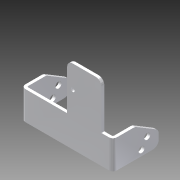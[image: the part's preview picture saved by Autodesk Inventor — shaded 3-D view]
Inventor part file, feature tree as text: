
AUTODESK INVENTOR PART (.ipt)
format: ipt  version: 2014 SP1 (Build 180222100, 222)  size: 293,888 bytes
history: native  units: in
note: dims shown in document units (in); Inventor stores cm internally (conversion verified against a paired STEP export)
features: other x8, sketch x5, sheet_metal_op x3, chamfer x2
ambient origin geometry x8: Origin, YZ Plane, XZ Plane, XY Plane, X Axis, Y Axis, Z Axis, Center Point
bodies: Solid1 (feature_tree)
feature tree (18):
  sheet_metal_op  "Face1"
  sheet_metal_op  "Flange1"
  chamfer  "Corner Round1"
  chamfer  "Corner Round2"
  sketch  "Sketch1"  dims[d0=0.155in]
  other  "Plate1"
  sketch  "Sketch2"  dims[d1=2.0in]
  other  "Plate2"
  sheet_metal_op  "Bend1"
  other  "mSketch3"
  sketch  "Sketch4"  dims[d3=1.25in]
  sketch  "Sketch5"  dims[d4=3.75in]
  sketch  "Sketch6"  dims[d6=0.375in d7=1.5in d8=0.25in d9=1.0in d10=0.125in d11=0.125in d12=0.0625in d13=0.25in d14=0.125in d15=2.0in d16=90.0deg d17=0.05in d18=0.5in d19=0.125in d20=0.125in d21=0.25in d22=0.266in d23=0.5in d24=0.125in d25=0.0in d26=0.266in d27=0.5in d28=0.125in d29=0.0in d30=0.75in d31=0.25in d32=0.266in d33=0.75in d34=0.25in d35=0.875in d36=0.625in d37=1.1811in d39=1.25in d40=0.3937in d42=1.0in d44=0.125in d45=0.0in d46=0.125in d47=0.0in d48=0.25in d2=0.25in d5=0.25in]
  other  "Cut1"
  other  "Cut2"
  other  "Cut3"
  other  "Cut4"
  other  "Definition1"
